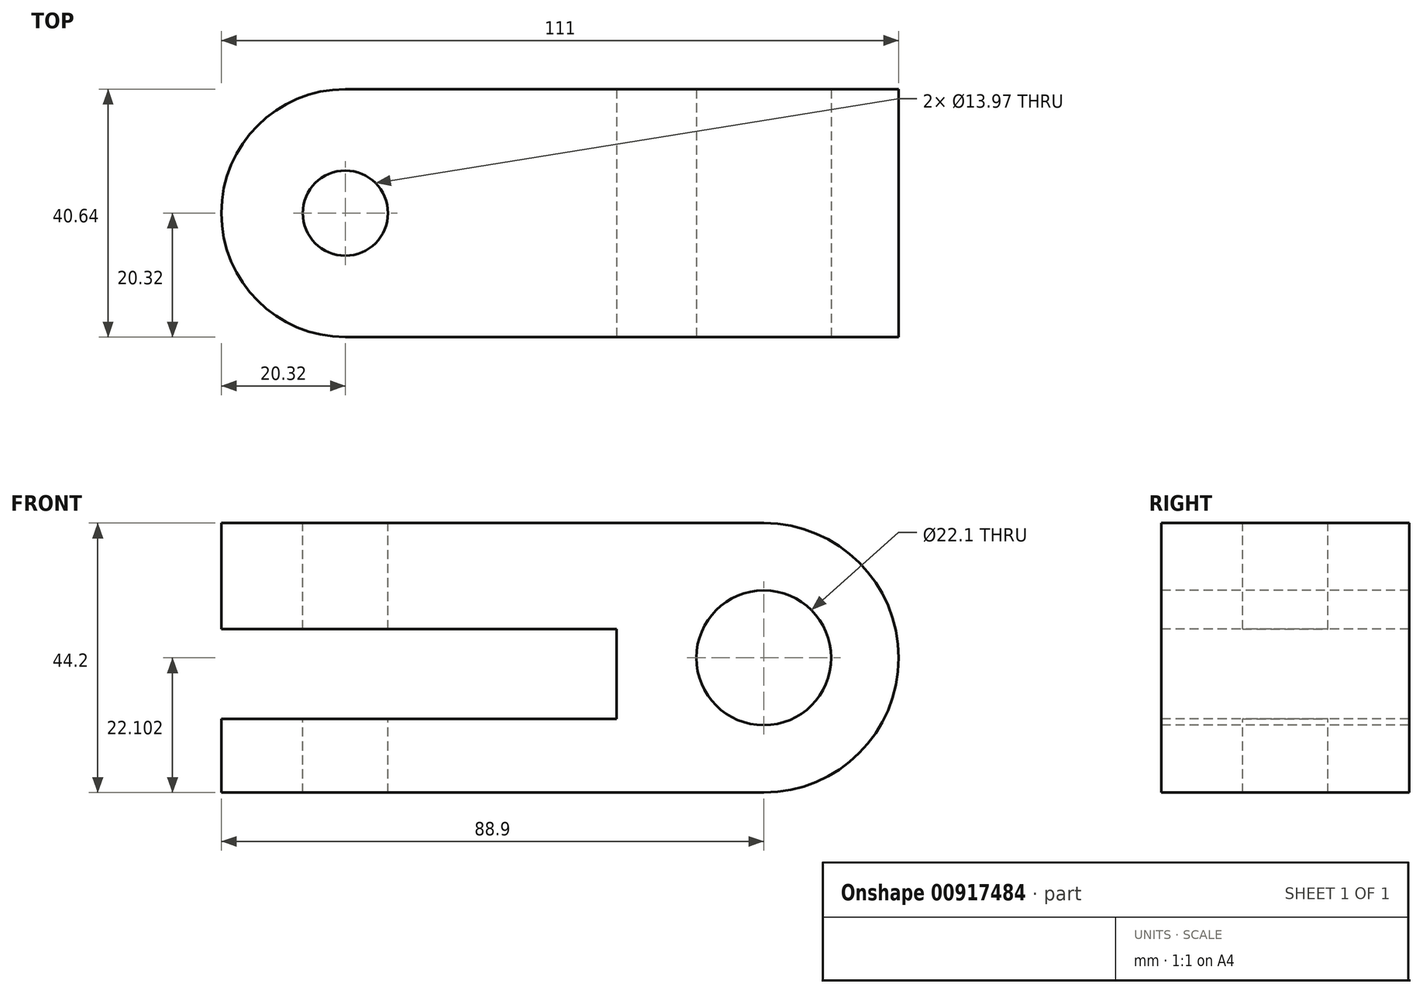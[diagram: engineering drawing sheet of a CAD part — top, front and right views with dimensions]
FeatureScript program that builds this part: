
annotation { "Feature Type Name" : "Feature", "Feature Type Description" : "" }
export const myFeature = defineFeature(function(context is Context, id is Id, definition is map)
    precondition{}
    {
        {
            var Q0;
            Q0=qCreatedBy(makeId("Front.planeOp"),FACE);
            var sketch = newSketch(context, id + "F0", { "sketchPlane" : qUnion([Q0])});
            skLineSegment(sketch, "E0.bottom", {"start": v(0, 0) * mm, "end": v(68.58, 0) * mm});
            skLineSegment(sketch, "E0.top", {"start": v(0, -44.2) * mm, "end": v(68.58, -44.2) * mm});
            skLineSegment(sketch, "E0.left", {"start": v(0, 0) * mm, "end": v(0, -44.2) * mm});
            skLineSegment(sketch, "E0.right", {"start": v(68.58, 0) * mm, "end": v(68.58, -44.2) * mm});
            skCircle(sketch, "E1", {"center": v(68.58, -22.1) * mm, "radius": 22.1 * mm});
            skSolve(sketch);
        }
        {
            var Q0;
            Q0 = qSketchRegion(id + "F0", true);
            extrude(context, id + "F1", {"entities" : qUnion([Q0]), "depth" : 40.64 * mm, "offsetDistance" : 25.4 * mm});
        }
        {
            var Q0;
            Q0=makeQuery(id+"F1.opExtrude","SWEPT_FACE",FACE,{"disambiguationData":[OSD([sQuery(id+"F0.wireOp",EDGE,"E0.bottom")])]});
            var sketch = newSketch(context, id + "F2", { "sketchPlane" : qUnion([Q0])});
            skCircle(sketch, "E2", {"center": v(0, -20.32) * mm, "radius": 20.32 * mm});
            skSolve(sketch);
        }
        {
            var Q0;
            {var subQ1=sQuery(id+"F0.wireOp",EDGE,"E0.bottom");var subQ2=makeQuery(id+"F1.opExtrude","SWEPT_EDGE",EDGE,{"disambiguationData":[OSD([subQ1,sQuery(id+"F0.wireOp",EDGE,"E0.left")])]});Q0=makeQuery(id+"F2.imprint","IMPRINT",FACE,{"disambiguationData":[TD([[makeQuery(id+"F2.imprint","IMPRINT",EDGE,{"derivedFrom":subQ2}),1.0]])]});}
            extrude(context, id + "F3", {"entities" : qUnion([Q0]), "operationType" : NewBodyOperationType.ADD, "oppositeDirection" : true, "depth" : 44.2 * mm, "offsetDistance" : 25.4 * mm});
        }
        {
            var Q0;
            Q0=makeQuery(id+"F1.opExtrude","CAP_FACE",FACE,{"disambiguationData":[OSD([sQuery(id+"F0.wireOp",EDGE,"E0.bottom"),sQuery(id+"F0.wireOp",EDGE,"E0.top"),sQuery(id+"F0.wireOp",EDGE,"E0.left"),sQuery(id+"F0.wireOp",EDGE,"E1")])],"isStart":false});
            var sketch = newSketch(context, id + "F4", { "sketchPlane" : qUnion([Q0])});
            skLineSegment(sketch, "E3.bottom", {"start": v(44.45, -17.4) * mm, "end": v(0, -17.4) * mm});
            skLineSegment(sketch, "E3.top", {"start": v(44.45, -32.13) * mm, "end": v(0, -32.13) * mm});
            skLineSegment(sketch, "E3.left", {"start": v(44.45, -17.4) * mm, "end": v(44.45, -32.13) * mm});
            skLineSegment(sketch, "E3.right", {"start": v(0, -17.4) * mm, "end": v(0, -32.13) * mm});
            skSolve(sketch);
        }
        {
            var Q0;
            Q0 = qSketchRegion(id + "F4", true);
            extrude(context, id + "F5", {"entities" : qUnion([Q0]), "operationType" : NewBodyOperationType.REMOVE, "endBound" : BoundingType.THROUGH_ALL, "oppositeDirection" : true, "depth" : 25.4 * mm, "offsetDistance" : 25.4 * mm});
        }
        {
            var Q0;
            Q0=makeQuery(id+"F1.opExtrude","CAP_FACE",FACE,{"disambiguationData":[OSD([sQuery(id+"F0.wireOp",EDGE,"E0.bottom"),sQuery(id+"F0.wireOp",EDGE,"E0.top"),sQuery(id+"F0.wireOp",EDGE,"E0.left"),sQuery(id+"F0.wireOp",EDGE,"E1")])],"isStart":false});
            var sketch = newSketch(context, id + "F6", { "sketchPlane" : qUnion([Q0])});
            skLineSegment(sketch, "E4", {"start": v(0, -17.4) * mm, "end": v(-20.32, -17.4) * mm});
            skLineSegment(sketch, "E5", {"start": v(0, -32.13) * mm, "end": v(-20.32, -32.13) * mm});
            skLineSegment(sketch, "E6.bottom", {"start": v(-20.32, -17.4) * mm, "end": v(0, -17.4) * mm});
            skLineSegment(sketch, "E6.top", {"start": v(-20.32, -32.13) * mm, "end": v(0, -32.13) * mm});
            skLineSegment(sketch, "E6.left", {"start": v(-20.32, -17.4) * mm, "end": v(-20.32, -32.13) * mm});
            skLineSegment(sketch, "E6.right", {"start": v(0, -17.4) * mm, "end": v(0, -32.13) * mm});
            skSolve(sketch);
        }
        {
            var Q0;
            Q0 = qSketchRegion(id + "F6", true);
            extrude(context, id + "F7", {"entities" : qUnion([Q0]), "operationType" : NewBodyOperationType.REMOVE, "endBound" : BoundingType.THROUGH_ALL, "oppositeDirection" : true, "depth" : 25.4 * mm, "offsetDistance" : 25.4 * mm});
        }
        {
            var Q0;
            {var subQ0=sQuery(id+"F0.wireOp",EDGE,"E0.bottom");Q0=makeQuery(id+"F3.boolean.opBoolean","MERGE",FACE,{"derivedFrom":[makeQuery(id+"F1.opExtrude","SWEPT_FACE",FACE,{"disambiguationData":[OSD([subQ0])]}),makeQuery(id+"F3.opExtrude","CAP_FACE",FACE,{"disambiguationData":[OSD([subQ0,sQuery(id+"F0.wireOp",EDGE,"E0.left"),sQuery(id+"F2.wireOp",EDGE,"E2")])],"isStart":true})]});}
            var sketch = newSketch(context, id + "F8", { "sketchPlane" : qUnion([Q0])});
            skLineSegment(sketch, "E7", {"start": v(0, -40.64) * mm, "end": v(0, 0) * mm});
            skCircle(sketch, "E8", {"center": v(0, -20.32) * mm, "radius": 6.99 * mm});
            skSolve(sketch);
        }
        {
            var Q0;
            Q0 = qSketchRegion(id + "F8", true);
            extrude(context, id + "F9", {"entities" : qUnion([Q0]), "operationType" : NewBodyOperationType.REMOVE, "endBound" : BoundingType.THROUGH_ALL, "oppositeDirection" : true, "depth" : 25.4 * mm, "offsetDistance" : 25.4 * mm});
        }
        {
            var Q0;
            Q0=makeQuery(id+"F1.opExtrude","CAP_FACE",FACE,{"disambiguationData":[OSD([sQuery(id+"F0.wireOp",EDGE,"E0.bottom"),sQuery(id+"F0.wireOp",EDGE,"E0.top"),sQuery(id+"F0.wireOp",EDGE,"E0.left"),sQuery(id+"F0.wireOp",EDGE,"E1")])],"isStart":false});
            var sketch = newSketch(context, id + "F10", { "sketchPlane" : qUnion([Q0])});
            skLineSegment(sketch, "E9", {"start": v(68.58, 0) * mm, "end": v(68.58, -44.2) * mm});
            skCircle(sketch, "E10", {"center": v(68.58, -22.1) * mm, "radius": 11.05 * mm});
            skSolve(sketch);
        }
        {
            var Q0;
            Q0 = qSketchRegion(id + "F10", true);
            extrude(context, id + "F11", {"entities" : qUnion([Q0]), "operationType" : NewBodyOperationType.REMOVE, "endBound" : BoundingType.THROUGH_ALL, "oppositeDirection" : true, "depth" : 25.4 * mm, "offsetDistance" : 25.4 * mm});
        }
    });
